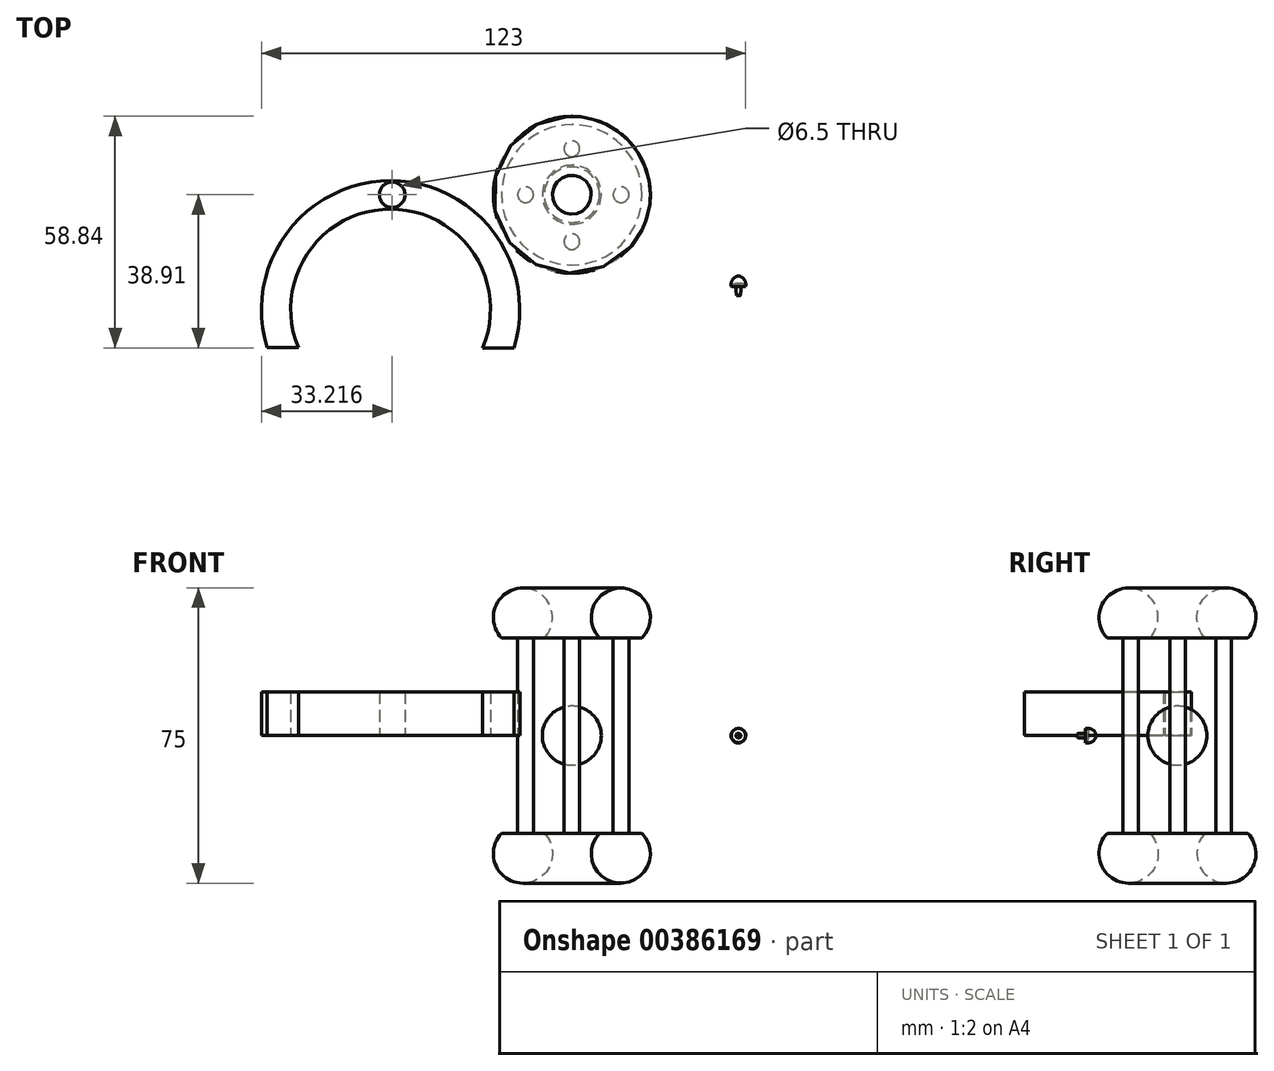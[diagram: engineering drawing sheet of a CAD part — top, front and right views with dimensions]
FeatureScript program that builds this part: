
annotation { "Feature Type Name" : "Feature", "Feature Type Description" : "" }
export const myFeature = defineFeature(function(context is Context, id is Id, definition is map)
    precondition{}
    {
        {
            var Q0;
            Q0=qCreatedBy(makeId("Front.planeOp"),FACE);
            var sketch = newSketch(context, id + "F0", { "sketchPlane" : qUnion([Q0])});
            skCircle(sketch, "E0", {"center": v(12.43, -30) * mm, "radius": 7.5 * mm});
            skLineSegment(sketch, "E1", {"start": v(7.03, -24.8) * mm, "end": v(17.84, -24.8) * mm});
            skLineSegment(sketch, "E2", {"start": v(0, 23.88) * mm, "end": v(0, -56.45) * mm, "construction": true});
            skSolve(sketch);
        }
        {
            var Q0;
            {var subQ0=sQuery(id+"F0.wireOp",EDGE,"E1");Q0=makeQuery(id+"F0.imprint","IMPRINT",FACE,{"disambiguationData":[TD([[makeQuery(id+"F0.imprint","IMPRINT",EDGE,{"derivedFrom":subQ0}),-1.0]])]});}
            var Q1;
            Q1=sQuery(id+"F0.wireOp",EDGE,"E2");
            revolve(context, id + "F1", {"entities" : qUnion([Q0]), "axis" : qUnion([Q1]), "revolveType" : RevolveType.FULL});
        }
        {
            var Q0;
            Q0=makeQuery(id+"F1.opRevolve","SWEPT_BODY",BODY,{"disambiguationData":[OSD([sQuery(id+"F0.wireOp",EDGE,"E0"),sQuery(id+"F0.wireOp",EDGE,"E1")])]});
            var Q1;
            Q1=qCreatedBy(makeId("Top.planeOp"),FACE);
            mirror(context, id + "F2", {"entities" : qUnion([Q0]), "mirrorPlane" : qUnion([Q1])});
        }
        {
            var Q0;
            Q0=makeQuery(id+"F1.opRevolve","SWEPT_FACE",FACE,{"disambiguationData":[OSD([sQuery(id+"F0.wireOp",EDGE,"E1")])]});
            var sketch = newSketch(context, id + "F3", { "sketchPlane" : qUnion([Q0])});
            skCircle(sketch, "E3", {"center": v(12.51, 0) * mm, "radius": 2 * mm});
            skCircle(sketch, "E4", {"center": v(0, -11.93) * mm, "radius": 2 * mm});
            skCircle(sketch, "E5", {"center": v(-11.75, 0) * mm, "radius": 2 * mm});
            skCircle(sketch, "E6", {"center": v(0, 11.7) * mm, "radius": 2 * mm});
            skSolve(sketch);
        }
        {
            var Q0;
            Q0=makeQuery(id+"F3.imprint","IMPRINT",FACE,{"disambiguationData":[TD([[makeQuery(id+"F3.imprint","IMPRINT",EDGE,{"derivedFrom":sQuery(id+"F3.wireOp",EDGE,"E6")}),1.0]])]});
            var Q1;
            Q1=makeQuery(id+"F3.imprint","IMPRINT",FACE,{"disambiguationData":[TD([[makeQuery(id+"F3.imprint","IMPRINT",EDGE,{"derivedFrom":sQuery(id+"F3.wireOp",EDGE,"E3")}),1.0]])]});
            var Q2;
            Q2=makeQuery(id+"F3.imprint","IMPRINT",FACE,{"disambiguationData":[TD([[makeQuery(id+"F3.imprint","IMPRINT",EDGE,{"derivedFrom":sQuery(id+"F3.wireOp",EDGE,"E4")}),1.0]])]});
            var Q3;
            Q3=makeQuery(id+"F3.imprint","IMPRINT",FACE,{"disambiguationData":[TD([[makeQuery(id+"F3.imprint","IMPRINT",EDGE,{"derivedFrom":sQuery(id+"F3.wireOp",EDGE,"E5")}),1.0]])]});
            var Q4;
            Q4=makeQuery(id+"F2.opPattern","COPY",FACE,{"derivedFrom":makeQuery(id+"F1.opRevolve","SWEPT_FACE",FACE,{"disambiguationData":[OSD([sQuery(id+"F0.wireOp",EDGE,"E1")])]}),"instanceName":"1"});
            extrude(context, id + "F4", {"entities" : qUnion([Q0, Q1, Q2, Q3]), "operationType" : NewBodyOperationType.ADD, "endBound" : BoundingType.UP_TO_SURFACE, "endBoundEntityFace" : qUnion([Q4]), "depth" : 33.9 * mm, "hasSecondDirection" : true, "secondDirectionOppositeDirection" : true, "secondDirectionDepth" : 0.5 * mm});
        }
        {
            var Q0;
            Q0=qCreatedBy(makeId("Top.planeOp"),FACE);
            var sketch = newSketch(context, id + "F5", { "sketchPlane" : qUnion([Q0])});
            skLineSegment(sketch, "E7", {"start": v(0, -7.5) * mm, "end": v(0, 7.5) * mm});
            skPoint(sketch, "E8", {"position": v(0, 0) * mm});
            skArc(sketch, "E9", {"start": v(0, 7.5) * mm, "mid": v(7.5, 0) * mm, "end": v(0, -7.5) * mm});
            skSolve(sketch);
        }
        {
            var Q0;
            Q0=makeQuery(id+"F5.imprint","IMPRINT",FACE,{"disambiguationData":[TD([[makeQuery(id+"F5.imprint","IMPRINT",EDGE,{"derivedFrom":sQuery(id+"F5.wireOp",EDGE,"E7")}),-1.0]])]});
            var Q1;
            Q1=sQuery(id+"F5.wireOp",EDGE,"E7");
            revolve(context, id + "F6", {"operationType" : NewBodyOperationType.ADD, "entities" : qUnion([Q0]), "axis" : qUnion([Q1]), "revolveType" : RevolveType.FULL});
        }
        {
            var Q0;
            Q0=qCreatedBy(makeId("Top.planeOp"),FACE);
            var sketch = newSketch(context, id + "F7", { "sketchPlane" : qUnion([Q0])});
            skArc(sketch, "E10", {"start": v(-14.67, -38.9) * mm, "mid": v(-46.03, 3.56) * mm, "end": v(-77.43, -38.87) * mm});
            skLineSegment(sketch, "E11", {"start": v(-77.43, -38.87) * mm, "end": v(-69.43, -38.87) * mm});
            skLineSegment(sketch, "E12", {"start": v(-14.67, -38.9) * mm, "end": v(-22.67, -38.9) * mm});
            skArc(sketch, "E13", {"start": v(-22.67, -38.9) * mm, "mid": v(-46.03, -3.64) * mm, "end": v(-69.43, -38.87) * mm});
            skCircle(sketch, "E14", {"center": v(-45.65, 0) * mm, "radius": 3.25 * mm});
            skSolve(sketch);
        }
        {
            var Q0;
            Q0=makeQuery(id+"F7.imprint","IMPRINT",FACE,{"disambiguationData":[TD([[makeQuery(id+"F7.imprint","IMPRINT",EDGE,{"derivedFrom":sQuery(id+"F7.wireOp",EDGE,"E10")}),1.0]])]});
            extrude(context, id + "F8", {"entities" : qUnion([Q0]), "depth" : 11.1 * mm});
        }
        {
            var Q0;
            Q0=qCreatedBy(makeId("Top.planeOp"),FACE);
            var sketch = newSketch(context, id + "F9", { "sketchPlane" : qUnion([Q0])});
            skLineSegment(sketch, "E15", {"start": v(42.33, -20.61) * mm, "end": v(42.33, -25.61) * mm});
            skPoint(sketch, "E16.startSnap0", {"position": v(42.33, -23.11) * mm});
            skArc(sketch, "E17", {"start": v(44.13, -23.37) * mm, "mid": v(43.83, -21.6) * mm, "end": v(42.33, -20.61) * mm});
            skArc(sketch, "E18", {"start": v(44.13, -23.37) * mm, "mid": v(43.6, -22.7) * mm, "end": v(42.77, -22.62) * mm});
            skLineSegment(sketch, "E19", {"start": v(42.33, -25.61) * mm, "end": v(42.77, -25.61) * mm});
            skArc(sketch, "E20", {"start": v(42.77, -25.61) * mm, "mid": v(42.94, -24.12) * mm, "end": v(42.77, -22.62) * mm});
            skLineSegment(sketch, "E21", {"start": v(48.52, -11.14) * mm, "end": v(48.52, -16.14) * mm});
            skPoint(sketch, "E22.startSnap0", {"position": v(48.52, -13.64) * mm});
            skArc(sketch, "E23", {"start": v(50.3, -14.34) * mm, "mid": v(50.23, -12.29) * mm, "end": v(48.52, -11.14) * mm});
            skArc(sketch, "E24", {"start": v(50.3, -14.34) * mm, "mid": v(49.76, -13.68) * mm, "end": v(48.92, -13.6) * mm});
            skArc(sketch, "E25", {"start": v(48.92, -16.59) * mm, "mid": v(49.1, -15.1) * mm, "end": v(48.92, -13.6) * mm});
            skArc(sketch, "E26", {"start": v(48.92, -16.59) * mm, "mid": v(48.8, -16.3) * mm, "end": v(48.52, -16.15) * mm});
            skSolve(sketch);
        }
        {
            var Q0;
            Q0=makeQuery(id+"F9.imprint","IMPRINT",FACE,{"disambiguationData":[TD([[makeQuery(id+"F9.imprint","IMPRINT",EDGE,{"derivedFrom":sQuery(id+"F9.wireOp",EDGE,"E15")}),1.0]])]});
            var Q1;
            Q1=sQuery(id+"F9.wireOp",EDGE,"E15");
            revolve(context, id + "F10", {"entities" : qUnion([Q0]), "axis" : qUnion([Q1]), "revolveType" : RevolveType.FULL});
        }
    });
